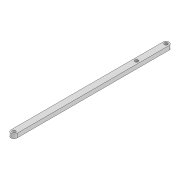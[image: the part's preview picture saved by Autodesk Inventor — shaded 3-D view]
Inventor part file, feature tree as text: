
AUTODESK INVENTOR PART (.ipt)
format: ipt  version: 2022 (Build 260153000, 153)  size: 92,160 bytes
history: native  units: mm
features: extrude x1, sketch x1
ambient origin geometry x8: Origin, YZ Plane, XZ Plane, XY Plane, X Axis, Y Axis, Z Axis, Center Point
bodies: Solid1 (feature_tree)
feature tree (2):
  extrude  "Extrusion1"  Depth=120.259mm
  sketch  "Sketch1"  dims[d0=3.2mm d1=3.2mm d2=6.0mm d3=149.325mm d6=4.0mm d7=0.0mm d14=3.2mm d15=120.259mm]
